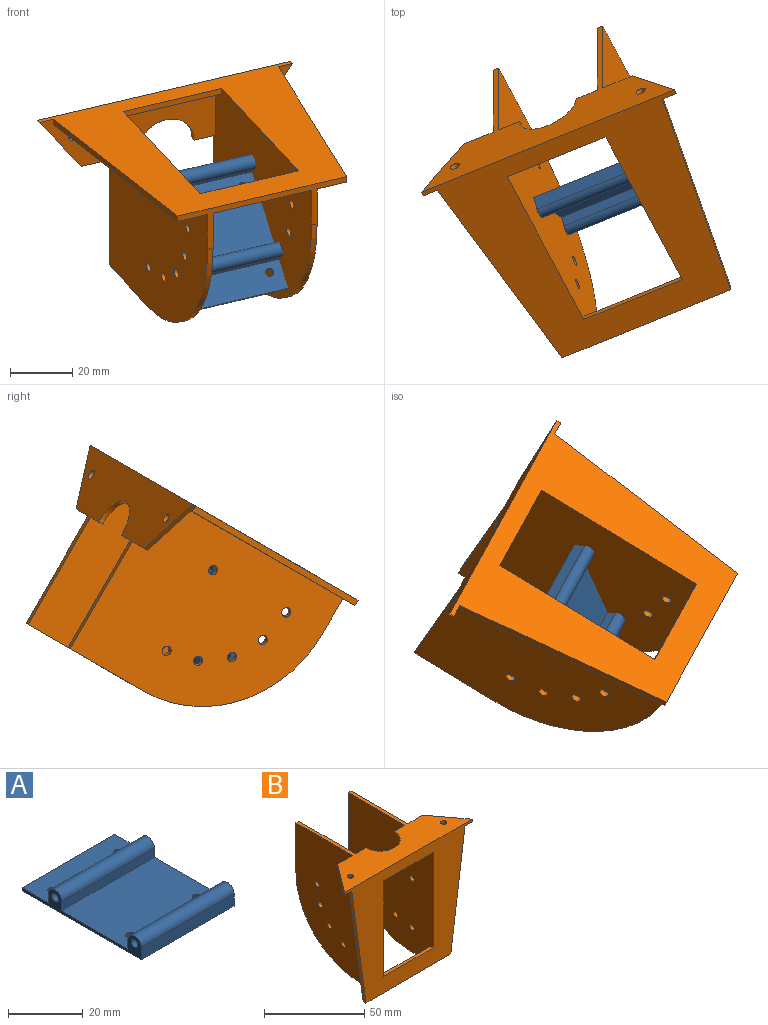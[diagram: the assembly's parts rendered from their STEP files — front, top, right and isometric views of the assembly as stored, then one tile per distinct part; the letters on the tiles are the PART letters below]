
ASSEMBLY  parts=2 mates=1
PART A: 18 faces, bbox 35x45x6.5 mm
  f0: plane 35x10mm, normal (0,0,1), area 339.4mm2, adj f2,f4,f6,f12,f15,f17
  f1: plane 35x25mm, normal (0,0,1), area 864.4mm2, adj f5,f6,f8,f11,f16,f17
  f2: plane 35x1mm, normal (0,1,0), area 35mm2, adj f0,f6,f7,f17
  f3: plane 35x4mm, normal (0,-1,0), area 140mm2, adj f6,f7,f9,f17
  f4: cylinder r=1.3mm len=2.6mm, axis (0,0,-1), area 8.2mm2, adj f0,f7
  f5: cylinder r=1.3mm len=2.6mm, axis (0,0,-1), area 8.2mm2, adj f1,f7
  f6: plane 45x6.5mm, normal (1,0,0), area 84.8mm2, adj f0,f1,f2,f3,f7,f8,f9,f10
  f7: plane 45x35mm, normal (0,0,-1), area 1553.8mm2, adj f2,f3,f4,f5,f6,f15,f16,f17
  f8: plane 35x3mm, normal (0,1,0), area 105mm2, adj f1,f6,f9,f17
  f9: cylinder r=2.5mm len=35mm, axis (1,0,0), area 274.9mm2, adj f3,f6,f8,f17
  f10: cylinder r=1.25mm len=35mm, axis (1,0,0), area 274.9mm2, adj f6,f17
  f11: plane 35x3mm, normal (0,-1,0), area 105mm2, adj f1,f6,f13,f17
  f12: plane 35x3mm, normal (0,1,0), area 105mm2, adj f0,f6,f13,f17
  f13: cylinder r=2.5mm len=35mm, axis (1,0,0), area 274.9mm2, adj f6,f11,f12,f17
  f14: cylinder r=1.25mm len=35mm, axis (1,0,0), area 274.9mm2, adj f6,f17
  f15: cylinder r=1.3mm len=2.6mm, axis (0,0,-1), area 8.2mm2, adj f0,f7
  f16: cylinder r=1.3mm len=2.6mm, axis (0,0,-1), area 8.2mm2, adj f1,f7
  f17: plane 45x6.5mm, normal (-1,0,0), area 84.8mm2, adj f0,f1,f2,f3,f7,f8,f9,f10
PART B: 43 faces, bbox 90x60x75 mm
  f0: plane 35x18mm, normal (0,0,-1), area 472.9mm2, adj f3,f4,f9,f22,f28,f29
  f1: plane 25.5x20mm, normal (0,0,-1), area 311mm2, adj f2,f5,f6,f7,f8,f24,f25
  f2: plane 75x58mm, normal (1,0,0), area 3843.1mm2, adj f1,f7,f10,f11,f12,f13,f14,f15
  f3: plane 75x60mm, normal (-1,0,0), area 3960.1mm2, adj f0,f4,f5,f10,f11,f12,f13,f14
  f4: plane 7.5x1.5mm, normal (0,1,0), area 11.3mm2, adj f0,f3,f9,f10
  f5: plane 90x75mm, normal (0,-1,0), area 3232.5mm2, adj f1,f3,f6,f10,f19,f20,f23,f24
  f6: plane 20x15mm, normal (0.8,0.6,0), area 37.5mm2, adj f1,f5,f7,f10
  f7: plane 10.5x1.5mm, normal (0,1,0), area 15.8mm2, adj f1,f2,f6,f10
  f8: cylinder r=1.6mm len=3.2mm, axis (0,0,1), area 15.1mm2, adj f1,f10
  f9: cylinder r=10mm len=20mm, axis (0,0,1), area 47.1mm2, adj f0,f4,f10,f29
  f10: plane 90x60mm, normal (0,0,1), area 1486.8mm2, adj f2,f3,f4,f5,f6,f7,f8,f9
  f11: cylinder r=45mm len=45mm, axis (-1,0,0), area 141.4mm2, adj f2,f3,f12,f19
  f12: plane 30x2mm, normal (0,1,0), area 60mm2, adj f2,f3,f10,f11
  f13: cylinder r=1.55mm len=3.1mm, axis (-1,0,0), area 19.5mm2, adj f2,f3
  f14: cylinder r=1.55mm len=3.1mm, axis (-1,0,0), area 19.5mm2, adj f2,f3
  f15: cylinder r=1.55mm len=3.1mm, axis (-1,0,0), area 19.5mm2, adj f2,f3
  f16: cylinder r=1.55mm len=3.1mm, axis (-1,0,0), area 19.5mm2, adj f2,f3
  f17: cylinder r=1.55mm len=3.1mm, axis (-1,0,0), area 19.5mm2, adj f2,f3
  f18: cylinder r=1.55mm len=3.1mm, axis (-1,0,0), area 19.5mm2, adj f2,f3
  f19: plane 60x15mm, normal (0,0,-1), area 172mm2, adj f2,f3,f5,f11,f21,f24,f25,f27
  f20: plane 35x2mm, normal (0,0,1), area 70mm2, adj f3,f5,f21,f28
  f21: plane 35x10mm, normal (0,1,0), area 350mm2, adj f3,f19,f20,f28
  f22: plane 35x5mm, normal (0,1,0), area 175mm2, adj f0,f3,f23,f28
  f23: plane 35x2mm, normal (0,0,-1), area 70mm2, adj f3,f5,f22,f28
  f24: plane 73.5x10mm, normal (0.99,0,-0.13), area 148.4mm2, adj f1,f5,f19,f25
  f25: plane 73.5x20.5mm, normal (0,1,0), area 1139.3mm2, adj f1,f2,f19,f24
  f26: plane 25.5x20mm, normal (0,0,-1), area 311mm2, adj f5,f27,f30,f31,f32,f41,f42
  f27: plane 75x58mm, normal (-1,0,0), area 3843.1mm2, adj f10,f19,f26,f31,f33,f34,f35,f36
  f28: plane 75x60mm, normal (1,0,0), area 3960.1mm2, adj f0,f5,f10,f19,f20,f21,f22,f23
  f29: plane 7.5x1.5mm, normal (0,1,0), area 11.3mm2, adj f0,f9,f10,f28
  f30: plane 20x15mm, normal (-0.8,0.6,0), area 37.5mm2, adj f5,f10,f26,f31
  f31: plane 10.5x1.5mm, normal (0,1,0), area 15.8mm2, adj f10,f26,f27,f30
  f32: cylinder r=1.6mm len=3.2mm, axis (0,0,1), area 15.1mm2, adj f10,f26
  f33: cylinder r=45mm len=45mm, axis (1,0,0), area 141.4mm2, adj f19,f27,f28,f34
  f34: plane 30x2mm, normal (0,1,0), area 60mm2, adj f10,f27,f28,f33
  f35: cylinder r=1.55mm len=3.1mm, axis (1,0,0), area 19.5mm2, adj f27,f28
  f36: cylinder r=1.55mm len=3.1mm, axis (1,0,0), area 19.5mm2, adj f27,f28
  f37: cylinder r=1.55mm len=3.1mm, axis (1,0,0), area 19.5mm2, adj f27,f28
  f38: cylinder r=1.55mm len=3.1mm, axis (1,0,0), area 19.5mm2, adj f27,f28
  f39: cylinder r=1.55mm len=3.1mm, axis (1,0,0), area 19.5mm2, adj f27,f28
  f40: cylinder r=1.55mm len=3.1mm, axis (1,0,0), area 19.5mm2, adj f27,f28
  f41: plane 73.5x10mm, normal (-0.99,0,-0.13), area 148.4mm2, adj f5,f19,f26,f42
  f42: plane 73.5x20.5mm, normal (0,1,0), area 1139.3mm2, adj f19,f26,f27,f41
PLACE A rot(axis=(-0.03,0.62,-0.79),155.3deg) t=(-7.32,20.26,-31.7)mm
PLACE B rot(axis=(-0.91,-0.35,0.2),64.5deg) t=(-25.06,36.08,14.65)mm
MATE revolute A.f9 <-> B.f11  axis (-0.91,-0.37,-0.21) through (-27.79,13.81,-15.53)mm
